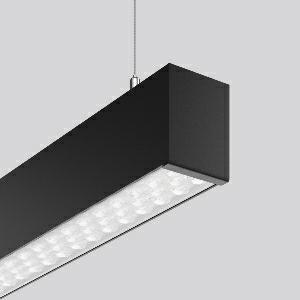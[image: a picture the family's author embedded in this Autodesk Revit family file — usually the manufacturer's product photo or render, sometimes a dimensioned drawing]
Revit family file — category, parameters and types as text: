
# Revit family: linedo_single_ip20_312563_003_9712
name_source: partatom
category: Lighting Fixtures
units: mm (PartAtom-declared; Revit-internal decimal feet)

## family parameters
Cut with Voids When Loaded = No
Host = Face
Light Source = No
Part Type = Normal
Room Calculation Point = No
Round Connector Dimension = Use Diameter
Shared = No

## types (1)
- LINEDO single IP20 (1 x LED Modul 830, 4550 lm, 3000)
    Apparent Load = 31 VA
    CIE Flux Codes = 86 96 99 100 100
    Color Rendering = 80
    Color Temperature = 3000
    Default Elevation = 1800 mm
    Description = Series: LINEDO single IP20
Stylish pendant luminaire. Housing: extruded aluminium profile, powder-coated. End cap aluminium powder-coated, without visible screws. High-efficiency LED units with optimum light control thanks to clear plastic (PC) lens optics. 2-point steel cable suspension freely positionable and infinitely height-adjustable. With power cord (2.5 m). Please order canopy separately if required. Perfect for office areas (RUG < 19) and environments with computer screens in accordance with EN 12464-1. 
Colour: deep black, matt (RAL 9005)
Length: 1700 mm
Width: 58 mm
Height: 76 mm
Suspension length: 100-1500 mm
Lamp: LED
Socket: without socket
Colour temperature: 3000K
Colour rendering index (CRI): 80
System power: 31 W
Rated luminous flux: 4550 lm
Beam angle Down: 59°
Luminous efficiency: 147 lm/W
Control gear: Regulated power supply
Protection class: I
Type of protection: IP 20
    Height = 76 mm
    Lamp = 1 x LED Modul 830
    Lamp Light Flux = 4550 lm
    Lamp count = 1
    Length = 1700 mm
    Lifetime = 50000 h
    Luminous efficacy = 147 lm/W
    Manufacturer = RZB
    ModVariant = No
    Model = 312563.003
    Mounting Place = Ceiling
    Mounting Type = Surface mounted, Pendant
    Number of Poles = 1
    OnlyDefault = Yes
    Power Factor = 1
    Product Name = LINEDO single IP20
    Product group = Pendant luminaires
    ProductGroupID = 902
    Protection Class = Protection class I
    Protection Degree = IP 20
    RLX_Detail_Level = 1
    RLX_Emergency_Light_Flux = 0 lm
    RLX_Emergency_Type = 0
    RLX_Emergency_Type_DB = No
    RlxData = <blob elided: 35017 chars, md5=a185684f>
    Socket = socket
    Standby Power = 0 W
    System Light Flux = 4550 lm
    System Power = 31 W
    Type Comments = ALEA SPOT
    Type Image = 312563.003.jpg
    URL = http://relux.com
    VarID = ---
    Voltage = 230 V
    Voltage Range = 220-240 V
    Weight = 0.00 kg
    Width = 58 mm

## geometry (parser evidence)
native form markers: Blend x4, Sweep x10
no freeform markers — native parametric forms only
